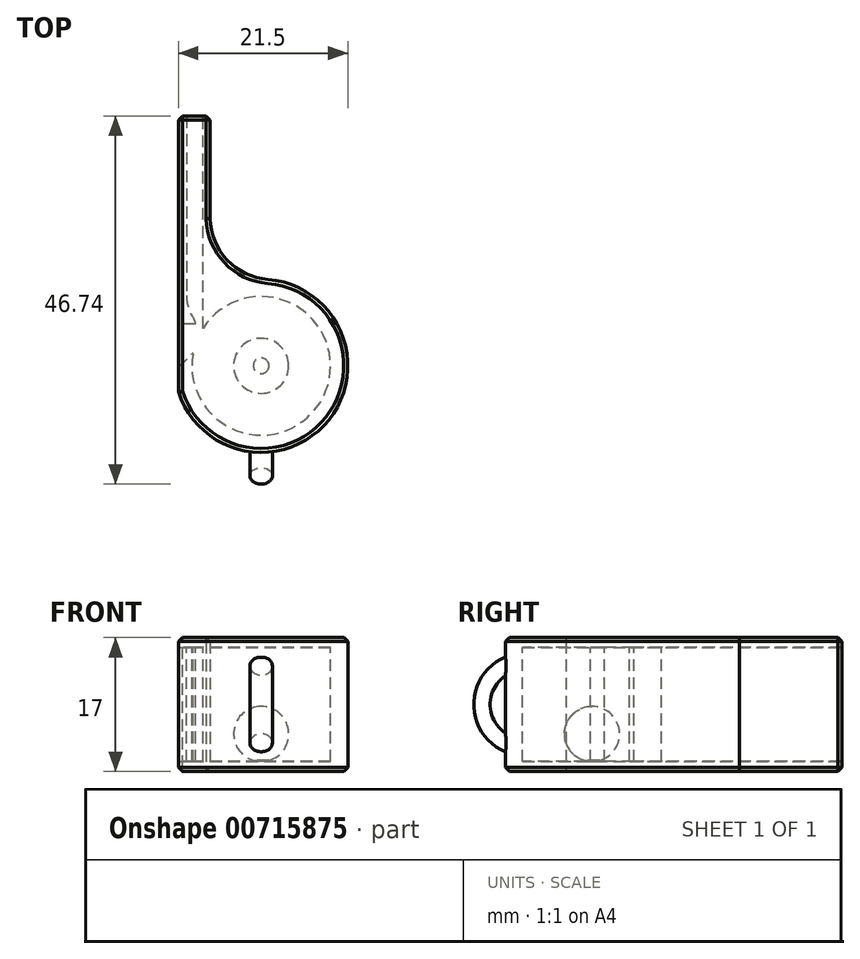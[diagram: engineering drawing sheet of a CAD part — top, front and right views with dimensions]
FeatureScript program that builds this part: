
annotation { "Feature Type Name" : "Feature", "Feature Type Description" : "" }
export const myFeature = defineFeature(function(context is Context, id is Id, definition is map)
    precondition{}
    {
        {
            var Q0;
            Q0=qCreatedBy(makeId("Top.planeOp"),FACE);
            var sketch = newSketch(context, id + "F0", { "sketchPlane" : qUnion([Q0])});
            skArc(sketch, "E0.0.4", {"start": v(-10.5, -3.28) * mm, "mid": v(8.6, -6.86) * mm, "end": v(0.87, 10.97) * mm});
            skLineSegment(sketch, "E0.0.3", {"start": v(-10.5, 31.72) * mm, "end": v(-10.5, -3.28) * mm});
            skLineSegment(sketch, "E0.0.2", {"start": v(-6.5, 31.72) * mm, "end": v(-10.5, 31.72) * mm});
            skLineSegment(sketch, "E0.0.1", {"start": v(-6.5, 18.72) * mm, "end": v(-6.5, 31.72) * mm});
            skArc(sketch, "E0.0.0", {"start": v(0.87, 10.97) * mm, "mid": v(-4.3, 13.43) * mm, "end": v(-6.5, 18.72) * mm});
            skSolve(sketch);
        }
        {
            var Q0;
            Q0=makeQuery(id+"F0.imprint","IMPRINT",FACE,{"disambiguationData":[TD([[makeQuery(id+"F0.imprint","IMPRINT",EDGE,{"derivedFrom":sQuery(id+"F0.wireOp",EDGE,"E0.0.4")}),1.0]])]});
            extrude(context, id + "F1", {"entities" : qUnion([Q0]), "endBound" : BoundingType.SYMMETRIC, "depth" : 17 * mm});
        }
        {
            var Q0;
            Q0=qCreatedBy(makeId("Top.planeOp"),FACE);
            var sketch = newSketch(context, id + "F2", { "sketchPlane" : qUnion([Q0])});
            skLineSegment(sketch, "E1.0", {"start": v(-9.5, 31.72) * mm, "end": v(-9.5, 8.92) * mm});
            skLineSegment(sketch, "E2.0", {"start": v(-7.4, 4.76) * mm, "end": v(-7.4, 31.72) * mm});
            skArc(sketch, "E3.0", {"start": v(-8.67, 1.53) * mm, "mid": v(8.2, -3.2) * mm, "end": v(-7.4, 4.76) * mm});
            skLineSegment(sketch, "E4.0", {"start": v(-10.5, -0.18) * mm, "end": v(-8.75, 1.57) * mm});
            skArc(sketch, "E5.0", {"start": v(-8.57, 6.02) * mm, "mid": v(-9.26, 7.4) * mm, "end": v(-9.5, 8.92) * mm});
            skArc(sketch, "E6.0", {"start": v(-8.35, 5.32) * mm, "mid": v(-8.4, 5.69) * mm, "end": v(-8.57, 6.02) * mm});
            skLineSegment(sketch, "E7.0", {"start": v(-8.35, 5.32) * mm, "end": v(-10.5, 5.32) * mm});
            skLineSegment(sketch, "E8", {"start": v(-7.4, 31.72) * mm, "end": v(-9.5, 31.72) * mm});
            skLineSegment(sketch, "E9", {"start": v(-10.5, 5.32) * mm, "end": v(-10.5, -0.18) * mm});
            skPoint(sketch, "E10.visualSharp", {"position": v(-8.64, 1.68) * mm});
            skArc(sketch, "E10.filletArc", {"start": v(-8.67, 1.53) * mm, "mid": v(-8.7, 1.58) * mm, "end": v(-8.75, 1.57) * mm});
            skSolve(sketch);
        }
        {
            var Q0;
            Q0=makeQuery(id+"F2.imprint","IMPRINT",FACE,{"disambiguationData":[TD([[makeQuery(id+"F2.imprint","IMPRINT",EDGE,{"derivedFrom":sQuery(id+"F2.wireOp",EDGE,"E1.0")}),1.0]])]});
            extrude(context, id + "F3", {"entities" : qUnion([Q0]), "operationType" : NewBodyOperationType.REMOVE, "endBound" : BoundingType.SYMMETRIC, "oppositeDirection" : true, "depth" : 14.5 * mm, "offsetDistance" : 25 * mm});
        }
        {
            var Q0;
            Q0=qCreatedBy(makeId("Right.planeOp"),FACE);
            var sketch = newSketch(context, id + "F4", { "sketchPlane" : qUnion([Q0])});
            skArc(sketch, "E11", {"start": v(0, -7.25) * mm, "mid": v(3.5, -3.75) * mm, "end": v(0, -0.25) * mm});
            skLineSegment(sketch, "E12.0", {"start": v(-8.8, -7.25) * mm, "end": v(8.8, -7.25) * mm, "construction": true});
            skLineSegment(sketch, "E13", {"start": v(0, 3.94) * mm, "end": v(0, -16.8) * mm, "construction": true});
            skLineSegment(sketch, "E14", {"start": v(0, -7.25) * mm, "end": v(0, -0.25) * mm});
            skSolve(sketch);
        }
        {
            var Q0;
            Q0=makeQuery(id+"F4.imprint","IMPRINT",FACE,{"disambiguationData":[TD([[makeQuery(id+"F4.imprint","IMPRINT",EDGE,{"derivedFrom":sQuery(id+"F4.wireOp",EDGE,"E11")}),1.0]])]});
            var Q1;
            Q1=sQuery(id+"F4.wireOp",EDGE,"E11");
            var Q2;
            Q2=sQuery(id+"F4.wireOp",EDGE,"E13");
            revolve(context, id + "F5", {"entities" : qUnion([Q0]), "surfaceEntities" : qUnion([Q1]), "axis" : qUnion([Q2]), "revolveType" : RevolveType.FULL});
        }
        {
            var Q0;
            Q0=makeQuery(id+"F3.boolean.opBoolean","COPY",FACE,{"derivedFrom":makeQuery(id+"F3.opExtrude","CAP_FACE",FACE,{"disambiguationData":[OSD([sQuery(id+"F2.wireOp",EDGE,"E1.0"),sQuery(id+"F2.wireOp",EDGE,"E2.0"),sQuery(id+"F2.wireOp",EDGE,"E3.0"),sQuery(id+"F2.wireOp",EDGE,"E4.0"),sQuery(id+"F2.wireOp",EDGE,"E5.0"),sQuery(id+"F2.wireOp",EDGE,"E6.0"),sQuery(id+"F2.wireOp",EDGE,"E7.0"),sQuery(id+"F2.wireOp",EDGE,"E8"),sQuery(id+"F2.wireOp",EDGE,"E9"),sQuery(id+"F2.wireOp",EDGE,"E10.filletArc")])],"isStart":false})});
            var sketch = newSketch(context, id + "F6", { "sketchPlane" : qUnion([Q0])});
            skCircle(sketch, "E15", {"center": v(0, 0) * mm, "radius": 1 * mm});
            skSolve(sketch);
        }
        {
            var Q0;
            Q0=qSketchRegion(id+"F6",true);
            extrude(context, id + "F7", {"entities" : qUnion([Q0]), "operationType" : NewBodyOperationType.ADD, "depth" : 2 * mm});
        }
        {
            var Q0;
            Q0=makeQuery(id+"F1.opExtrude","CAP_EDGE",EDGE,{"disambiguationData":[OSD([sQuery(id+"F0.wireOp",EDGE,"E0.0.3")])],"isStart":false});
            var Q1;
            Q1=makeQuery(id+"F1.opExtrude","CAP_EDGE",EDGE,{"disambiguationData":[OSD([sQuery(id+"F0.wireOp",EDGE,"E0.0.0")])],"isStart":true});
            var Q2;
            Q2=makeQuery(id+"F1.opExtrude","CAP_EDGE",EDGE,{"disambiguationData":[OSD([sQuery(id+"F0.wireOp",EDGE,"E0.0.4")])],"isStart":false});
            var Q3;
            Q3=makeQuery(id+"F1.opExtrude","CAP_EDGE",EDGE,{"disambiguationData":[OSD([sQuery(id+"F0.wireOp",EDGE,"E0.0.3")])],"isStart":true});
            var Q4;
            Q4=makeQuery(id+"F1.opExtrude","CAP_EDGE",EDGE,{"disambiguationData":[OSD([sQuery(id+"F0.wireOp",EDGE,"E0.0.1")])],"isStart":false});
            var Q5;
            Q5=makeQuery(id+"F1.opExtrude","CAP_EDGE",EDGE,{"disambiguationData":[OSD([sQuery(id+"F0.wireOp",EDGE,"E0.0.0")])],"isStart":false});
            var Q6;
            Q6=makeQuery(id+"F1.opExtrude","CAP_EDGE",EDGE,{"disambiguationData":[OSD([sQuery(id+"F0.wireOp",EDGE,"E0.0.4")])],"isStart":true});
            var Q7;
            Q7=makeQuery(id+"F1.opExtrude","CAP_EDGE",EDGE,{"disambiguationData":[OSD([sQuery(id+"F0.wireOp",EDGE,"E0.0.1")])],"isStart":true});
            var Q8;
            Q8=makeQuery(id+"F1.opExtrude","SWEPT_EDGE",EDGE,{"disambiguationData":[OSD([sQuery(id+"F0.wireOp",EDGE,"E0.0.3"),sQuery(id+"F0.wireOp",EDGE,"E0.0.2")])]});
            var Q9;
            Q9=makeQuery(id+"F1.opExtrude","CAP_EDGE",EDGE,{"disambiguationData":[OSD([sQuery(id+"F0.wireOp",EDGE,"E0.0.2")])],"isStart":false});
            var Q10;
            Q10=makeQuery(id+"F1.opExtrude","SWEPT_EDGE",EDGE,{"disambiguationData":[OSD([sQuery(id+"F0.wireOp",EDGE,"E0.0.2"),sQuery(id+"F0.wireOp",EDGE,"E0.0.1")])]});
            var Q11;
            Q11=makeQuery(id+"F1.opExtrude","CAP_EDGE",EDGE,{"disambiguationData":[OSD([sQuery(id+"F0.wireOp",EDGE,"E0.0.2")])],"isStart":true});
            chamfer(context, id + "F8", {"entities" : qUnion([Q0, Q1, Q2, Q3, Q4, Q5, Q6, Q7, Q8, Q9, Q10, Q11]), "width" : .5 * mm, "tangentPropagation" : true});
        }
        {
            var Q0;
            Q0=qCreatedBy(makeId("Top.planeOp"),FACE);
            var sketch = newSketch(context, id + "F9", { "sketchPlane" : qUnion([Q0])});
            skEllipse(sketch, "E16", {"center": v(0, -13.98) * mm, "majorRadius": 1.43 * mm, "minorRadius": 1.04 * mm, "majorAxis": v(-1, 0)});
            skLineSegment(sketch, "E17", {"start": v(-10.46, -8.51) * mm, "end": v(11.75, -8.51) * mm, "construction": true});
            skSolve(sketch);
        }
        {
            var Q0;
            Q0=makeQuery(id+"F9.imprint","IMPRINT",FACE,{"disambiguationData":[TD([[makeQuery(id+"F9.imprint","IMPRINT",EDGE,{"derivedFrom":sQuery(id+"F9.wireOp",EDGE,"E16")}),1.0]])]});
            var Q1;
            Q1=sQuery(id+"F9.wireOp",EDGE,"E17");
            revolve(context, id + "F10", {"operationType" : NewBodyOperationType.ADD, "surfaceOperationType" : NewSurfaceOperationType.NEW, "entities" : qUnion([Q0]), "axis" : qUnion([Q1]), "revolveType" : RevolveType.SYMMETRIC, "angle" : 144.57 * degree});
        }
    });
